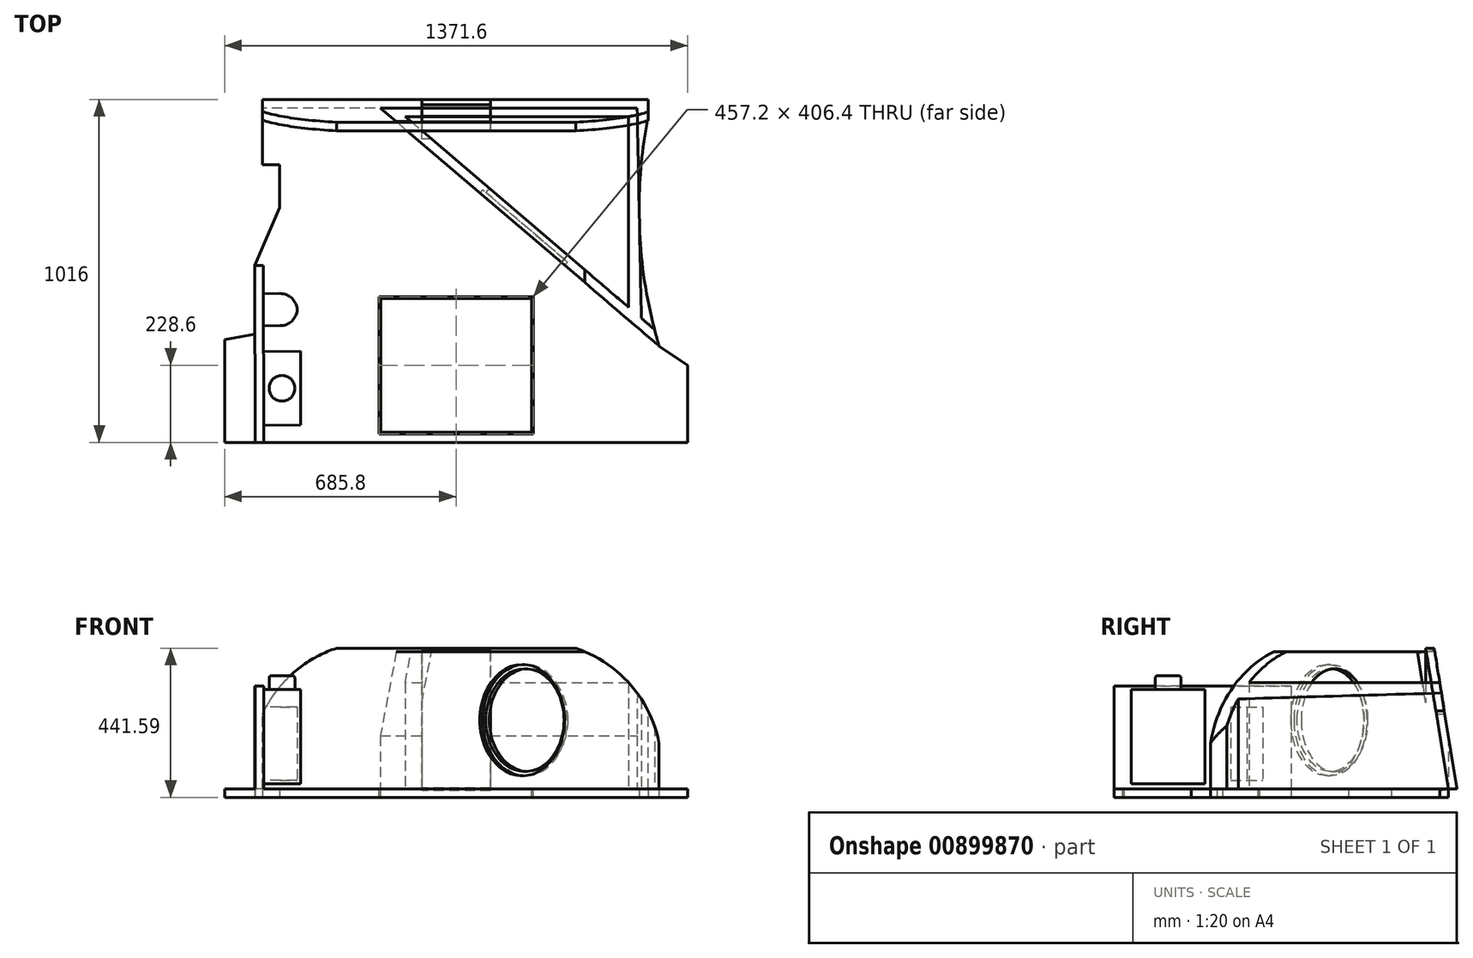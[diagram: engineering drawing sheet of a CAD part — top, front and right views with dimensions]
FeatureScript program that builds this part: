
annotation { "Feature Type Name" : "Feature", "Feature Type Description" : "" }
export const myFeature = defineFeature(function(context is Context, id is Id, definition is map)
    precondition{}
    {
        {
            var Q0;
            Q0=qCreatedBy(makeId("Top.planeOp"),FACE);
            var sketch = newSketch(context, id + "F0", { "sketchPlane" : qUnion([Q0])});
            skLineSegment(sketch, "E0.bottom", {"start": v(-574.04, 381) * mm, "end": v(568.96, 381) * mm});
            skLineSegment(sketch, "E1", {"start": v(-685.8, -609.6) * mm, "end": v(685.8, -609.6) * mm});
            skLineSegment(sketch, "E2", {"start": v(-685.8, -609.6) * mm, "end": v(-685.8, -304.8) * mm});
            skLineSegment(sketch, "E3", {"start": v(685.8, -381) * mm, "end": v(685.8, -609.6) * mm});
            skLineSegment(sketch, "E4", {"start": v(-685.8, -304.8) * mm, "end": v(-595.82, -288.52) * mm});
            skLineSegment(sketch, "E5", {"start": v(-595.82, -288.52) * mm, "end": v(-595.99, -85.32) * mm});
            skLineSegment(sketch, "E6", {"start": v(-574.04, 381) * mm, "end": v(-574.04, 212.59) * mm});
            skLineSegment(sketch, "E7", {"start": v(-574.04, 212.59) * mm, "end": v(-523.24, 212.59) * mm});
            skLineSegment(sketch, "E8", {"start": v(-523.24, 212.59) * mm, "end": v(-523.24, 85.59) * mm});
            skLineSegment(sketch, "E9", {"start": v(-523.24, 85.59) * mm, "end": v(-595.99, -85.32) * mm});
            skLineSegment(sketch, "E10", {"start": v(685.8, -381) * mm, "end": v(601.51, -324.27) * mm});
            skLineSegment(sketch, "E11", {"start": v(568.96, 381) * mm, "end": v(568.96, 355.6) * mm});
            skArc(sketch, "E12", {"start": v(568.96, 355.6) * mm, "mid": v(543.92, 13.68) * mm, "end": v(601.51, -324.27) * mm});
            skSolve(sketch);
        }
        {
            var Q0;
            Q0=qSketchRegion(id+"F0",true);
            extrude(context, id + "F1", {"entities" : qUnion([Q0]), "depth" : 25.4 * mm, "offsetDistance" : 25.4 * mm});
        }
        {
            var Q0;
            Q0=makeQuery(id+"F1.opExtrude","CAP_FACE",FACE,{"disambiguationData":[OSD([sQuery(id+"F0.wireOp",EDGE,"E0.bottom"),sQuery(id+"F0.wireOp",EDGE,"W605GUOn-W1BC-hpzk-du5D-lRq7CfKfPhlk"),sQuery(id+"F0.wireOp",EDGE,"BhcBOQm0-LC6C-naVo-rLmS-YFNbgF8lK3Yi"),sQuery(id+"F0.wireOp",EDGE,"E1"),sQuery(id+"F0.wireOp",EDGE,"E2"),sQuery(id+"F0.wireOp",EDGE,"u9wnJ2vL-7hmL-CWXn-YjCh-9UOyQw3PrTwL"),sQuery(id+"F0.wireOp",EDGE,"BANCc5qs-sGv9-K0Rv-eEJk-wrQsjLy7ADhK"),sQuery(id+"F0.wireOp",EDGE,"9mUNlxMa-Jzqg-L3WW-Beqh-AKG44Hujtvt8"),sQuery(id+"F0.wireOp",EDGE,"n7DAfoqq-sMU4-Jbp3-Y3Lt-S3jMFfcB2KZh"),sQuery(id+"F0.wireOp",EDGE,"F3p2CEnw-0ZHj-77iP-WJVi-9vjHXGPzvkfb"),sQuery(id+"F0.wireOp",EDGE,"ZNCwZrRp-HQCu-S5GE-EJ0A-Nfo9M3t5lMV9"),sQuery(id+"F0.wireOp",EDGE,"FQlTR5UO-ppFt-jqeN-joz0-pxmagkWIEg6L"),sQuery(id+"F0.wireOp",EDGE,"FQVYiaR8-DjGH-kJJ2-OJ1b-nRZnYTqOaLW2"),sQuery(id+"F0.wireOp",EDGE,"E3"),sQuery(id+"F0.wireOp",EDGE,"E4"),sQuery(id+"F0.wireOp",EDGE,"E5"),sQuery(id+"F0.wireOp",EDGE,"vCXjqmWP-xhdS-8qnO-hhTF-4SJ1CVbeM928"),sQuery(id+"F0.wireOp",EDGE,"HRn7fTde-drx0-yUOS-iL6b-0KnaToG7ZsJX")])],"isStart":false});
            var sketch = newSketch(context, id + "F2", { "sketchPlane" : qUnion([Q0])});
            skLineSegment(sketch, "E13.bottom", {"start": v(-228.6, -177.8) * mm, "end": v(228.6, -177.8) * mm});
            skLineSegment(sketch, "E13.top", {"start": v(-228.6, -584.2) * mm, "end": v(228.6, -584.2) * mm});
            skLineSegment(sketch, "E13.left", {"start": v(-228.6, -177.8) * mm, "end": v(-228.6, -584.2) * mm});
            skLineSegment(sketch, "E13.right", {"start": v(228.6, -177.8) * mm, "end": v(228.6, -584.2) * mm});
            skSolve(sketch);
        }
        {
            var Q0;
            Q0=qSketchRegion(id+"F2",true);
            extrude(context, id + "F3", {"entities" : qUnion([Q0]), "operationType" : NewBodyOperationType.REMOVE, "oppositeDirection" : true, "depth" : 25.4 * mm, "offsetDistance" : 25.4 * mm});
        }
        {
            var Q0;
            Q0=makeQuery(id+"F1.opExtrude","CAP_FACE",FACE,{"disambiguationData":[OSD([sQuery(id+"F0.wireOp",EDGE,"E0.bottom"),sQuery(id+"F0.wireOp",EDGE,"W605GUOn-W1BC-hpzk-du5D-lRq7CfKfPhlk"),sQuery(id+"F0.wireOp",EDGE,"BhcBOQm0-LC6C-naVo-rLmS-YFNbgF8lK3Yi"),sQuery(id+"F0.wireOp",EDGE,"E1"),sQuery(id+"F0.wireOp",EDGE,"E2"),sQuery(id+"F0.wireOp",EDGE,"u9wnJ2vL-7hmL-CWXn-YjCh-9UOyQw3PrTwL"),sQuery(id+"F0.wireOp",EDGE,"BANCc5qs-sGv9-K0Rv-eEJk-wrQsjLy7ADhK"),sQuery(id+"F0.wireOp",EDGE,"9mUNlxMa-Jzqg-L3WW-Beqh-AKG44Hujtvt8"),sQuery(id+"F0.wireOp",EDGE,"n7DAfoqq-sMU4-Jbp3-Y3Lt-S3jMFfcB2KZh"),sQuery(id+"F0.wireOp",EDGE,"F3p2CEnw-0ZHj-77iP-WJVi-9vjHXGPzvkfb"),sQuery(id+"F0.wireOp",EDGE,"ZNCwZrRp-HQCu-S5GE-EJ0A-Nfo9M3t5lMV9"),sQuery(id+"F0.wireOp",EDGE,"FQlTR5UO-ppFt-jqeN-joz0-pxmagkWIEg6L"),sQuery(id+"F0.wireOp",EDGE,"FQVYiaR8-DjGH-kJJ2-OJ1b-nRZnYTqOaLW2"),sQuery(id+"F0.wireOp",EDGE,"E3"),sQuery(id+"F0.wireOp",EDGE,"E4"),sQuery(id+"F0.wireOp",EDGE,"E5"),sQuery(id+"F0.wireOp",EDGE,"vCXjqmWP-xhdS-8qnO-hhTF-4SJ1CVbeM928"),sQuery(id+"F0.wireOp",EDGE,"HRn7fTde-drx0-yUOS-iL6b-0KnaToG7ZsJX")])],"isStart":false});
            var sketch = newSketch(context, id + "F4", { "sketchPlane" : qUnion([Q0])});
            skLineSegment(sketch, "E14.bottom", {"start": v(223.52, -182.88) * mm, "end": v(-223.52, -182.88) * mm});
            skLineSegment(sketch, "E14.top", {"start": v(223.52, -579.12) * mm, "end": v(-223.52, -579.12) * mm});
            skLineSegment(sketch, "E14.left", {"start": v(223.52, -182.88) * mm, "end": v(223.52, -579.12) * mm});
            skLineSegment(sketch, "E14.right", {"start": v(-223.52, -182.88) * mm, "end": v(-223.52, -579.12) * mm});
            skSolve(sketch);
        }
        {
            var Q0;
            Q0=qSketchRegion(id+"F4",true);
            extrude(context, id + "F5", {"entities" : qUnion([Q0]), "oppositeDirection" : true, "depth" : 25.4 * mm, "offsetDistance" : 25.4 * mm});
        }
        {
            var Q0;
            Q0=makeQuery(id+"F1.opExtrude","SWEPT_FACE",FACE,{"disambiguationData":[OSD([sQuery(id+"F0.wireOp",EDGE,"E6")])]});
            var sketch = newSketch(context, id + "F6", { "sketchPlane" : qUnion([Q0])});
            skLineSegment(sketch, "E15", {"start": v(-381, 25.4) * mm, "end": v(-313.45, 441.6) * mm});
            skLineSegment(sketch, "E16", {"start": v(-313.45, 441.6) * mm, "end": v(-338.85, 441.6) * mm});
            skLineSegment(sketch, "E17", {"start": v(-338.85, 441.6) * mm, "end": v(-406.4, 25.4) * mm});
            skLineSegment(sketch, "E18", {"start": v(-381, 25.4) * mm, "end": v(-406.4, 25.4) * mm});
            skSolve(sketch);
        }
        {
            var Q0;
            Q0 = qSketchRegion(id + "F6", true);
            extrude(context, id + "F7", {"entities" : qUnion([Q0]), "oppositeDirection" : true, "depth" : 1143 * mm, "offsetDistance" : 25.4 * mm});
        }
        {
            var Q0;
            {var subQ0=sQuery(id+"F0.wireOp",EDGE,"E11");var subQ1=sQuery(id+"F0.wireOp",EDGE,"E10");var subQ2=sQuery(id+"F0.wireOp",EDGE,"E8");var subQ3=sQuery(id+"F0.wireOp",EDGE,"E7");var subQ4=sQuery(id+"F0.wireOp",EDGE,"E6");var subQ5=sQuery(id+"F0.wireOp",EDGE,"E9");var subQ6=sQuery(id+"F0.wireOp",EDGE,"E0.bottom");var subQ7=sQuery(id+"F0.wireOp",EDGE,"E3");var subQ8=sQuery(id+"F0.wireOp",EDGE,"E1");var subQ9=sQuery(id+"F0.wireOp",EDGE,"E5");var subQ10=sQuery(id+"F0.wireOp",EDGE,"E12");Q0=makeQuery(id+"F21.boolean.opBoolean","SPLIT",FACE,{"disambiguationData":[TD([makeQuery(id+"F1.opExtrude","SWEPT_FACE",FACE,{"disambiguationData":[OSD([subQ6])]})])],"derivedFrom":makeQuery(id+"F1.opExtrude","CAP_FACE",FACE,{"disambiguationData":[OSD([subQ6,subQ8,sQuery(id+"F0.wireOp",EDGE,"E2"),subQ7,sQuery(id+"F0.wireOp",EDGE,"E4"),subQ9,subQ4,subQ3,subQ2,subQ5,subQ1,subQ0,subQ10])],"isStart":false})});}
            var sketch = newSketch(context, id + "F8", { "sketchPlane" : qUnion([Q0])});
            skLineSegment(sketch, "E19", {"start": v(-150.72, 355.6) * mm, "end": v(511.2, -209.64) * mm});
            skLineSegment(sketch, "E20", {"start": v(587.8, -275.04) * mm, "end": v(601.51, -324.27) * mm});
            skLineSegment(sketch, "E21", {"start": v(601.51, -324.27) * mm, "end": v(-224.4, 381) * mm});
            skLineSegment(sketch, "E22", {"start": v(-224.4, 381) * mm, "end": v(-180.46, 381) * mm});
            skLineSegment(sketch, "E23", {"start": v(536.6, 381) * mm, "end": v(511.2, 381) * mm});
            skLineSegment(sketch, "E24", {"start": v(511.2, 355.6) * mm, "end": v(511.2, -209.64) * mm});
            skLineSegment(sketch, "E25", {"start": v(511.2, 381) * mm, "end": v(-180.46, 381) * mm});
            skLineSegment(sketch, "E26", {"start": v(511.2, 355.6) * mm, "end": v(-150.72, 355.6) * mm});
            skLineSegment(sketch, "E27.trimOffspring", {"start": v(549.02, -241.93) * mm, "end": v(587.8, -275.04) * mm});
            skLineSegment(sketch, "E28", {"start": v(549.02, -241.93) * mm, "end": v(536.6, 381) * mm});
            skSolve(sketch);
        }
        {
            var Q0;
            Q0 = qSketchRegion(id + "F8", true);
            extrude(context, id + "F9", {"entities" : qUnion([Q0]), "depth" : 406.4 * mm, "offsetDistance" : 25.4 * mm});
        }
        {
            var Q0;
            Q0=makeQuery(id+"F7.opExtrude","CAP_FACE",FACE,{"disambiguationData":[OSD([sQuery(id+"F6.wireOp",EDGE,"E15"),sQuery(id+"F6.wireOp",EDGE,"E16"),sQuery(id+"F6.wireOp",EDGE,"E17"),sQuery(id+"F6.wireOp",EDGE,"E18")])],"isStart":true});
            var sketch = newSketch(context, id + "F10", { "sketchPlane" : qUnion([Q0])});
            skLineSegment(sketch, "E29", {"start": v(-406.4, 25.4) * mm, "end": v(-335.84, 460.16) * mm});
            skLineSegment(sketch, "E30", {"start": v(-335.84, 460.16) * mm, "end": v(-401.26, 460.16) * mm});
            skLineSegment(sketch, "E31", {"start": v(-401.26, 460.16) * mm, "end": v(-406.4, 25.4) * mm});
            skSolve(sketch);
        }
        {
            var Q0;
            Q0 = qSketchRegion(id + "F10", true);
            extrude(context, id + "F11", {"entities" : qUnion([Q0]), "operationType" : NewBodyOperationType.REMOVE, "oppositeDirection" : true, "depth" : 1143 * mm, "offsetDistance" : 25.4 * mm});
        }
        {
            var Q0;
            Q0=makeQuery(id+"F9.opExtrude","SWEPT_FACE",FACE,{"disambiguationData":[OSD([sQuery(id+"F8.wireOp",EDGE,"E21")])]});
            var sketch = newSketch(context, id + "F12", { "sketchPlane" : qUnion([Q0])});
            skCircle(sketch, "E32", {"center": v(134.6, 228.6) * mm, "radius": 165.1 * mm});
            skSolve(sketch);
        }
        {
            var Q0;
            Q0 = qSketchRegion(id + "F12", true);
            extrude(context, id + "F13", {"entities" : qUnion([Q0]), "operationType" : NewBodyOperationType.REMOVE, "oppositeDirection" : true, "depth" : 12.7 * mm, "offsetDistance" : 25.4 * mm});
        }
        {
            var Q0;
            Q0=makeQuery(id+"F13.boolean.opBoolean","COPY",FACE,{"derivedFrom":makeQuery(id+"F13.opExtrude","CAP_FACE",FACE,{"disambiguationData":[OSD([sQuery(id+"F12.wireOp",EDGE,"E32")])],"isStart":false})});
            var sketch = newSketch(context, id + "F14", { "sketchPlane" : qUnion([Q0])});
            skCircle(sketch, "E33", {"center": v(134.6, 228.6) * mm, "radius": 152.4 * mm});
            skSolve(sketch);
        }
        {
            var Q0;
            Q0 = qSketchRegion(id + "F14", true);
            extrude(context, id + "F15", {"entities" : qUnion([Q0]), "operationType" : NewBodyOperationType.REMOVE, "oppositeDirection" : true, "depth" : 25.4 * mm, "offsetDistance" : 25.4 * mm});
        }
        {
            var Q0;
            Q0=makeQuery(id+"F7.opExtrude","SWEPT_FACE",FACE,{"disambiguationData":[OSD([sQuery(id+"F6.wireOp",EDGE,"E17")])]});
            var sketch = newSketch(context, id + "F16", { "sketchPlane" : qUnion([Q0])});
            skLineSegment(sketch, "E34.bottom", {"start": v(-101.6, 376.52) * mm, "end": v(101.6, 376.52) * mm});
            skLineSegment(sketch, "E35", {"start": v(-101.6, -37.5) * mm, "end": v(101.6, -37.5) * mm});
            skLineSegment(sketch, "E36", {"start": v(101.6, 376.52) * mm, "end": v(101.6, -37.5) * mm});
            skLineSegment(sketch, "E37", {"start": v(-101.6, 376.52) * mm, "end": v(-101.6, -37.5) * mm});
            skSolve(sketch);
        }
        {
            var Q0;
            Q0 = qSketchRegion(id + "F16", true);
            extrude(context, id + "F17", {"entities" : qUnion([Q0]), "operationType" : NewBodyOperationType.REMOVE, "oppositeDirection" : true, "depth" : 50.8 * mm, "offsetDistance" : 25.4 * mm});
        }
        {
            var Q0;
            Q0=makeQuery(id+"F21.boolean.opBoolean","MERGE",FACE,{"derivedFrom":[makeQuery(id+"F1.opExtrude","SWEPT_FACE",FACE,{"disambiguationData":[OSD([sQuery(id+"F0.wireOp",EDGE,"E1")])]}),makeQuery(id+"F21.opExtrude","SWEPT_FACE",FACE,{"disambiguationData":[OSD([sQuery(id+"F20.wireOp",EDGE,"E50")])]})]});
            var sketch = newSketch(context, id + "F18", { "sketchPlane" : qUnion([Q0])});
            skLineSegment(sketch, "E38", {"start": v(566.9, 445.17) * mm, "end": v(342.9, 445.17) * mm});
            skLineSegment(sketch, "E39", {"start": v(566.9, 445.17) * mm, "end": v(605.92, 445.17) * mm});
            skLineSegment(sketch, "E40", {"start": v(605.92, 445.17) * mm, "end": v(605.92, 235.28) * mm});
            skLineSegment(sketch, "E41", {"start": v(605.92, 235.28) * mm, "end": v(605.92, 130.34) * mm});
            skArc(sketch, "E42", {"start": v(605.92, 130.34) * mm, "mid": v(522.22, 327.7) * mm, "end": v(342.9, 445.17) * mm});
            skLineSegment(sketch, "E43.MirrorCS", {"start": v(-566.9, 445.17) * mm, "end": v(-605.92, 445.17) * mm});
            skLineSegment(sketch, "E44.MirrorCS", {"start": v(-566.9, 445.17) * mm, "end": v(-342.9, 445.17) * mm});
            skArc(sketch, "E45.MirrorCS", {"start": v(-605.92, 130.34) * mm, "mid": v(-522.22, 327.7) * mm, "end": v(-342.9, 445.17) * mm});
            skLineSegment(sketch, "E46.MirrorCS", {"start": v(-605.92, 235.28) * mm, "end": v(-605.92, 130.34) * mm});
            skLineSegment(sketch, "E47.MirrorCS", {"start": v(-605.92, 445.17) * mm, "end": v(-605.92, 235.28) * mm});
            skSolve(sketch);
        }
        {
            var Q0;
            Q0 = qSketchRegion(id + "F18", true);
            extrude(context, id + "F19", {"entities" : qUnion([Q0]), "operationType" : NewBodyOperationType.REMOVE, "oppositeDirection" : true, "depth" : 990.6 * mm, "offsetDistance" : 25.4 * mm});
        }
        {
            var Q0;
            Q0=makeQuery(id+"F1.opExtrude","CAP_FACE",FACE,{"disambiguationData":[OSD([sQuery(id+"F0.wireOp",EDGE,"E0.bottom"),sQuery(id+"F0.wireOp",EDGE,"E1"),sQuery(id+"F0.wireOp",EDGE,"E2"),sQuery(id+"F0.wireOp",EDGE,"E3"),sQuery(id+"F0.wireOp",EDGE,"E4"),sQuery(id+"F0.wireOp",EDGE,"E5"),sQuery(id+"F0.wireOp",EDGE,"E6"),sQuery(id+"F0.wireOp",EDGE,"E7"),sQuery(id+"F0.wireOp",EDGE,"E8"),sQuery(id+"F0.wireOp",EDGE,"E9"),sQuery(id+"F0.wireOp",EDGE,"E10"),sQuery(id+"F0.wireOp",EDGE,"E11"),sQuery(id+"F0.wireOp",EDGE,"E12")])],"isStart":false});
            var sketch = newSketch(context, id + "F20", { "sketchPlane" : qUnion([Q0])});
            skLineSegment(sketch, "E48", {"start": v(-570.59, -85.32) * mm, "end": v(-595.99, -85.32) * mm});
            skLineSegment(sketch, "E49", {"start": v(-595.99, -85.32) * mm, "end": v(-595.56, -609.6) * mm});
            skLineSegment(sketch, "E50", {"start": v(-595.56, -609.6) * mm, "end": v(-570.28, -609.6) * mm});
            skLineSegment(sketch, "E51", {"start": v(-570.59, -85.32) * mm, "end": v(-570.28, -609.6) * mm});
            skSolve(sketch);
        }
        {
            var Q0;
            Q0 = qSketchRegion(id + "F20", true);
            extrude(context, id + "F21", {"entities" : qUnion([Q0]), "operationType" : NewBodyOperationType.ADD, "depth" : 304.8 * mm, "offsetDistance" : 25.4 * mm});
        }
        {
            var Q0;
            Q0=makeQuery(id+"F21.opExtrude","SWEPT_FACE",FACE,{"disambiguationData":[OSD([sQuery(id+"F20.wireOp",EDGE,"E51")])]});
            var sketch = newSketch(context, id + "F22", { "sketchPlane" : qUnion([Q0])});
            skLineSegment(sketch, "E52.bottom", {"start": v(-340.03, 320.04) * mm, "end": v(-558.47, 320.04) * mm});
            skLineSegment(sketch, "E52.top", {"start": v(-340.03, 40.64) * mm, "end": v(-558.47, 40.64) * mm});
            skLineSegment(sketch, "E52.left", {"start": v(-340.03, 320.04) * mm, "end": v(-340.03, 40.64) * mm});
            skLineSegment(sketch, "E52.right", {"start": v(-558.47, 320.04) * mm, "end": v(-558.47, 40.64) * mm});
            skSolve(sketch);
        }
        {
            var Q0;
            Q0 = qSketchRegion(id + "F22", true);
            extrude(context, id + "F23", {"entities" : qUnion([Q0]), "operationType" : NewBodyOperationType.ADD, "depth" : 109.22 * mm, "offsetDistance" : 25.4 * mm});
        }
        {
            var Q0;
            Q0=makeQuery(id+"F23.opExtrude","SWEPT_FACE",FACE,{"disambiguationData":[OSD([sQuery(id+"F22.wireOp",EDGE,"E52.bottom")])]});
            var sketch = newSketch(context, id + "F24", { "sketchPlane" : qUnion([Q0])});
            skCircle(sketch, "E53", {"center": v(-515.83, -449.52) * mm, "radius": 38.1 * mm});
            skPoint(sketch, "E53.centerSnap0", {"position": v(-515.83, -340.33) * mm});
            skPoint(sketch, "E53.centerSnap1", {"position": v(-461.16, -449.52) * mm});
            skSolve(sketch);
        }
        {
            var Q0;
            Q0 = qSketchRegion(id + "F24", true);
            extrude(context, id + "F25", {"entities" : qUnion([Q0]), "operationType" : NewBodyOperationType.ADD, "depth" : 40.64 * mm, "offsetDistance" : 25.4 * mm});
        }
        {
            var Q0;
            Q0=makeQuery(id+"F25.opExtrude","CAP_EDGE",EDGE,{"disambiguationData":[OSD([sQuery(id+"F24.wireOp",EDGE,"E53")])],"isStart":false});
            fillet(context, id + "F26", {"entities" : qUnion([Q0]), "radius" : 7.62 * mm, "tangentPropagation" : true, "allowEdgeOverflow" : false});
        }
        {
            var Q0;
            Q0=makeQuery(id+"F21.opExtrude","SWEPT_FACE",FACE,{"disambiguationData":[OSD([sQuery(id+"F20.wireOp",EDGE,"E51")])]});
            var sketch = newSketch(context, id + "F27", { "sketchPlane" : qUnion([Q0])});
            skLineSegment(sketch, "E54.bottom", {"start": v(-263.83, 267.46) * mm, "end": v(-168.58, 267.46) * mm});
            skLineSegment(sketch, "E54.top", {"start": v(-263.83, 50.8) * mm, "end": v(-168.58, 50.8) * mm});
            skLineSegment(sketch, "E54.left", {"start": v(-263.83, 267.46) * mm, "end": v(-263.83, 50.8) * mm});
            skLineSegment(sketch, "E54.right", {"start": v(-168.58, 267.46) * mm, "end": v(-168.58, 50.8) * mm});
            skSolve(sketch);
        }
        {
            var Q0;
            Q0 = qSketchRegion(id + "F27", true);
            extrude(context, id + "F28", {"entities" : qUnion([Q0]), "operationType" : NewBodyOperationType.ADD, "depth" : 99.82 * mm, "offsetDistance" : 25.4 * mm});
        }
        {
            var Q0;
            Q0=makeQuery(id+"F28.opExtrude","CAP_EDGE",EDGE,{"disambiguationData":[OSD([sQuery(id+"F27.wireOp",EDGE,"E54.right")])],"isStart":false});
            var Q1;
            Q1=makeQuery(id+"F28.opExtrude","CAP_EDGE",EDGE,{"disambiguationData":[OSD([sQuery(id+"F27.wireOp",EDGE,"E54.left")])],"isStart":false});
            fillet(context, id + "F29", {"entities" : qUnion([Q0, Q1]), "radius" : 50.8 * mm, "tangentPropagation" : true, "allowEdgeOverflow" : false});
        }
    });
